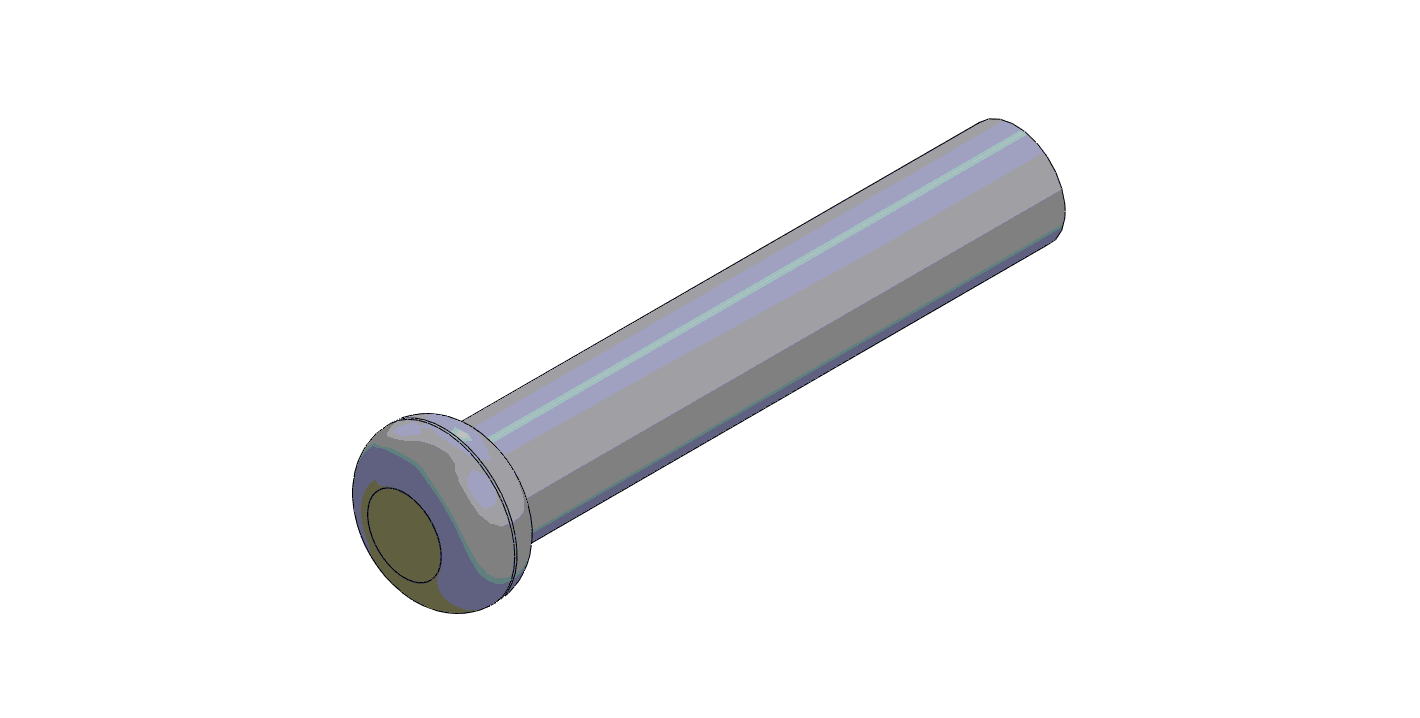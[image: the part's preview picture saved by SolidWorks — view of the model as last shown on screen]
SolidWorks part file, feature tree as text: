
SOLIDWORKS PART (.sldprt)
format: sldprt  version: not decoded by parser v0  size: 173,568 bytes
history: native  units: mm
features: sketch x2, extrude x2, material x1, fillet x1 (+12 scaffold rows collapsed)
feature tree (18):
  scaffold x12  (default folders/planes/origin — collapsed)
  material  "Material <not specified>"
  sketch  "Sketch1"  dims[D1=~9.060236mm]
  extrude  "Boss-Extrude1"  Depth=37.1348mm
  sketch  "Sketch2"  dims[D1=~6.490703mm]
  extrude  "Boss-Extrude2"  Depth=5.08mm
  fillet  "Fillet1"  Radius=2.54mm
decode coverage: 5 of 5 modeling features carry decoded parameters
note: ~ marks probable driven/reference dimensions
note: suppression state not decoded; provenance and decode notes live in map.json
